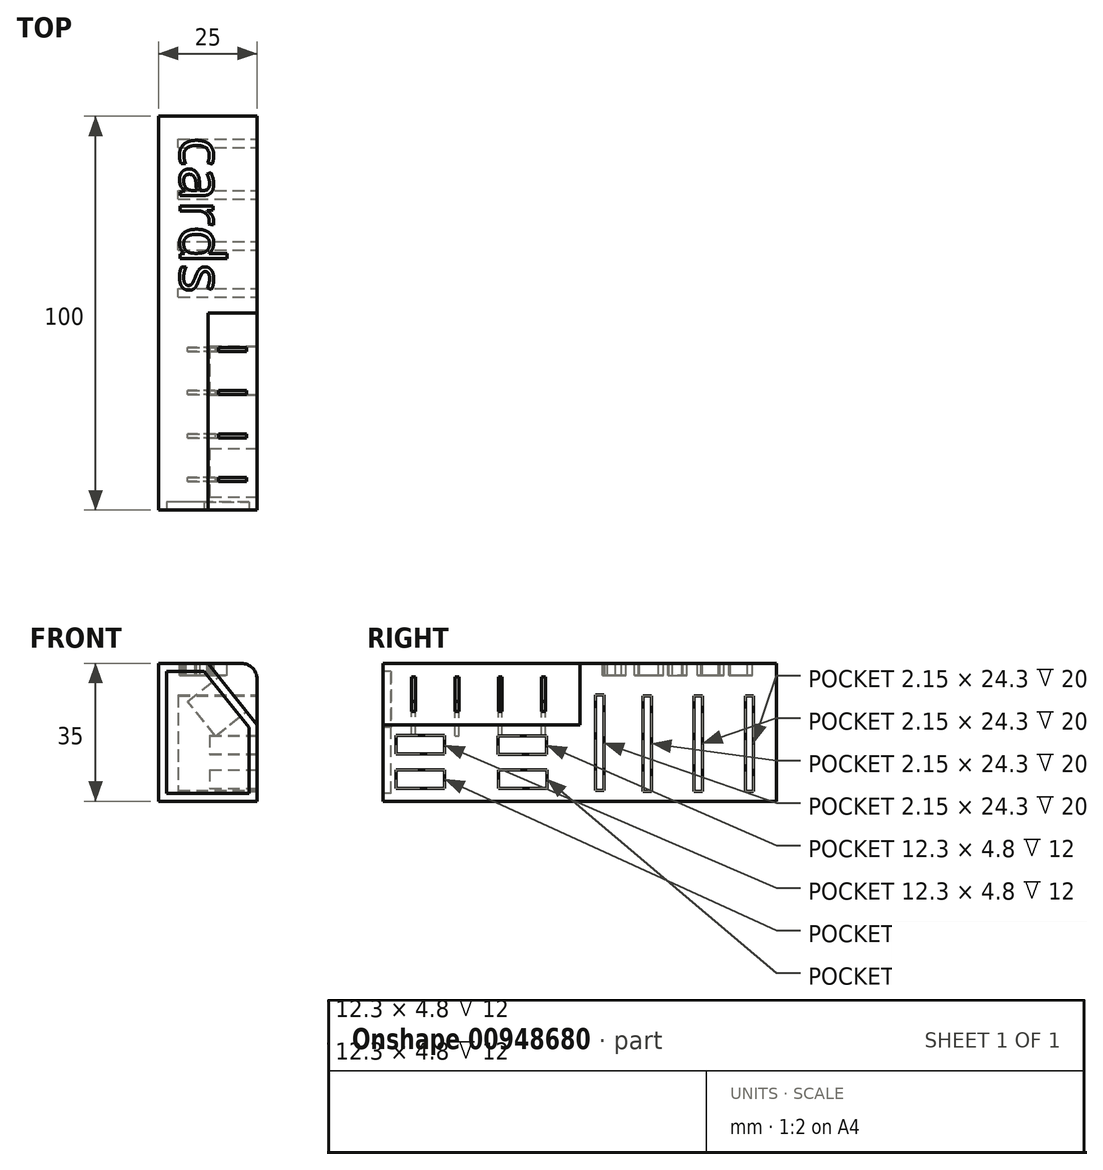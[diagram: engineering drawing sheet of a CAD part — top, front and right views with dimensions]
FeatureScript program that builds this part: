
annotation { "Feature Type Name" : "Feature", "Feature Type Description" : "" }
export const myFeature = defineFeature(function(context is Context, id is Id, definition is map)
    precondition{}
    {
        {
            var Q0;
            Q0=qCreatedBy(makeId("Top.planeOp"),FACE);
            var sketch = newSketch(context, id + "F0", { "sketchPlane" : qUnion([Q0])});
            skLineSegment(sketch, "E0.bottom", {"start": v(12.5, 50) * mm, "end": v(-12.5, 50) * mm});
            skLineSegment(sketch, "E0.top", {"start": v(12.5, -50) * mm, "end": v(-12.5, -50) * mm});
            skLineSegment(sketch, "E0.left", {"start": v(12.5, 50) * mm, "end": v(12.5, -50) * mm});
            skLineSegment(sketch, "E0.right", {"start": v(-12.5, 50) * mm, "end": v(-12.5, -50) * mm});
            skPoint(sketch, "E0.middle", {"position": v(0, 0) * mm});
            skSolve(sketch);
        }
        {
            var Q0;
            Q0=makeQuery(id+"F0.imprint","IMPRINT",FACE,{"disambiguationData":[TD([[makeQuery(id+"F0.imprint","IMPRINT",EDGE,{"derivedFrom":sQuery(id+"F0.wireOp",EDGE,"E0.bottom")}),1.0]])]});
            extrude(context, id + "F1", {"entities" : qUnion([Q0]), "oppositeDirection" : true, "depth" : 35 * mm, "offsetDistance" : 25 * mm});
        }
        {
            var Q0;
            Q0=makeQuery(id+"F1.opExtrude","SWEPT_FACE",FACE,{"disambiguationData":[OSD([sQuery(id+"F0.wireOp",EDGE,"E0.top")])]});
            var sketch = newSketch(context, id + "F2", { "sketchPlane" : qUnion([Q0])});
            skLineSegment(sketch, "E1", {"start": v(0, 0) * mm, "end": v(12.5, -15.61) * mm});
            skSolve(sketch);
        }
        {
            var Q0;
            {var subQ0=sQuery(id+"F2.wireOp",EDGE,"E1");Q0=makeQuery(id+"F2.imprint","IMPRINT",FACE,{"disambiguationData":[TD([[makeQuery(id+"F2.imprint","IMPRINT",EDGE,{"derivedFrom":subQ0}),1.0]])]});}
            extrude(context, id + "F3", {"entities" : qUnion([Q0]), "operationType" : NewBodyOperationType.REMOVE, "oppositeDirection" : true, "depth" : 50 * mm, "offsetDistance" : 25 * mm});
        }
        {
            var Q0;
            Q0=makeQuery(id+"F3.boolean.opBoolean","COPY",FACE,{"derivedFrom":makeQuery(id+"F3.opExtrude","SWEPT_FACE",FACE,{"disambiguationData":[OSD([sQuery(id+"F2.wireOp",EDGE,"E1")])]})});
            var sketch = newSketch(context, id + "F4", { "sketchPlane" : qUnion([Q0])});
            skLineSegment(sketch, "E2", {"start": v(-50, -10) * mm, "end": v(0, -10) * mm, "construction": true});
            skLineSegment(sketch, "E3.bottom", {"start": v(-9.72, -15.65) * mm, "end": v(-8.72, -15.65) * mm});
            skLineSegment(sketch, "E3.top", {"start": v(-9.72, -4.35) * mm, "end": v(-8.72, -4.35) * mm});
            skLineSegment(sketch, "E3.left", {"start": v(-9.72, -15.65) * mm, "end": v(-9.72, -4.35) * mm});
            skLineSegment(sketch, "E3.right", {"start": v(-8.72, -15.65) * mm, "end": v(-8.72, -4.35) * mm});
            skPoint(sketch, "E3.middle", {"position": v(-9.22, -10) * mm});
            skLineSegment(sketch, "E4.1.0.0", {"start": v(-20.72, -4.35) * mm, "end": v(-19.72, -4.35) * mm});
            skLineSegment(sketch, "E4.1.0.1", {"start": v(-19.72, -15.65) * mm, "end": v(-19.72, -4.35) * mm});
            skLineSegment(sketch, "E4.1.0.2", {"start": v(-20.72, -15.65) * mm, "end": v(-20.72, -4.35) * mm});
            skLineSegment(sketch, "E4.1.0.3", {"start": v(-20.72, -15.65) * mm, "end": v(-19.72, -15.65) * mm});
            skLineSegment(sketch, "E4.2.0.0", {"start": v(-31.72, -4.35) * mm, "end": v(-30.72, -4.35) * mm});
            skLineSegment(sketch, "E4.2.0.1", {"start": v(-30.72, -15.65) * mm, "end": v(-30.72, -4.35) * mm});
            skLineSegment(sketch, "E4.2.0.2", {"start": v(-31.72, -15.65) * mm, "end": v(-31.72, -4.35) * mm});
            skLineSegment(sketch, "E4.2.0.3", {"start": v(-31.72, -15.65) * mm, "end": v(-30.72, -15.65) * mm});
            skLineSegment(sketch, "E4.3.0.0", {"start": v(-42.72, -4.35) * mm, "end": v(-41.72, -4.35) * mm});
            skLineSegment(sketch, "E4.3.0.1", {"start": v(-41.72, -15.65) * mm, "end": v(-41.72, -4.35) * mm});
            skLineSegment(sketch, "E4.3.0.2", {"start": v(-42.72, -15.65) * mm, "end": v(-42.72, -4.35) * mm});
            skLineSegment(sketch, "E4.3.0.3", {"start": v(-42.72, -15.65) * mm, "end": v(-41.72, -15.65) * mm});
            skLineSegment(sketch, "E4.direction1", {"start": v(-9.72, -4.35) * mm, "end": v(-20.72, -4.35) * mm, "construction": true});
            skSolve(sketch);
        }
        {
            var Q0;
            Q0=makeQuery(id+"F4.imprint","IMPRINT",FACE,{"disambiguationData":[TD([[makeQuery(id+"F4.imprint","IMPRINT",EDGE,{"derivedFrom":sQuery(id+"F4.wireOp",EDGE,"E3.bottom")}),1.0]])]});
            var Q1;
            Q1=makeQuery(id+"F4.imprint","IMPRINT",FACE,{"disambiguationData":[TD([[makeQuery(id+"F4.imprint","IMPRINT",EDGE,{"derivedFrom":sQuery(id+"F4.wireOp",EDGE,"E4.1.0.0")}),-1.0]])]});
            var Q2;
            Q2=makeQuery(id+"F4.imprint","IMPRINT",FACE,{"disambiguationData":[TD([[makeQuery(id+"F4.imprint","IMPRINT",EDGE,{"derivedFrom":sQuery(id+"F4.wireOp",EDGE,"E4.2.0.0")}),-1.0]])]});
            var Q3;
            Q3=makeQuery(id+"F4.imprint","IMPRINT",FACE,{"disambiguationData":[TD([[makeQuery(id+"F4.imprint","IMPRINT",EDGE,{"derivedFrom":sQuery(id+"F4.wireOp",EDGE,"E4.3.0.0")}),-1.0]])]});
            extrude(context, id + "F5", {"entities" : qUnion([Q0, Q1, Q2, Q3]), "operationType" : NewBodyOperationType.REMOVE, "oppositeDirection" : true, "depth" : 10 * mm, "offsetDistance" : 25 * mm});
        }
        {
            var Q0;
            Q0=makeQuery(id+"F1.opExtrude","CAP_EDGE",EDGE,{"disambiguationData":[OSD([sQuery(id+"F0.wireOp",EDGE,"E0.left")])],"isStart":true});
            fillet(context, id + "F6", {"entities" : qUnion([Q0]), "radius" : 4 * mm, "tangentPropagation" : true, "allowEdgeOverflow" : false});
        }
        {
            var Q0;
            Q0=makeQuery(id+"F1.opExtrude","SWEPT_FACE",FACE,{"disambiguationData":[OSD([sQuery(id+"F0.wireOp",EDGE,"E0.left")])]});
            var sketch = newSketch(context, id + "F7", { "sketchPlane" : qUnion([Q0])});
            skLineSegment(sketch, "E5.bottom", {"start": v(42.02, -8.21) * mm, "end": v(44.17, -8.21) * mm});
            skLineSegment(sketch, "E5.top", {"start": v(42.02, -32.51) * mm, "end": v(44.17, -32.51) * mm});
            skLineSegment(sketch, "E5.left", {"start": v(42.02, -8.21) * mm, "end": v(42.02, -32.51) * mm});
            skLineSegment(sketch, "E5.right", {"start": v(44.17, -8.21) * mm, "end": v(44.17, -32.51) * mm});
            skPoint(sketch, "E5.middle", {"position": v(43.1, -20.36) * mm});
            skLineSegment(sketch, "E6.bottom", {"start": v(-34.37, -27) * mm, "end": v(-46.67, -27) * mm});
            skLineSegment(sketch, "E6.top", {"start": v(-34.37, -31.8) * mm, "end": v(-46.67, -31.8) * mm});
            skLineSegment(sketch, "E6.left", {"start": v(-34.37, -27) * mm, "end": v(-34.37, -31.8) * mm});
            skLineSegment(sketch, "E6.right", {"start": v(-46.67, -27) * mm, "end": v(-46.67, -31.8) * mm});
            skPoint(sketch, "E6.middle", {"position": v(-40.52, -29.4) * mm});
            skLineSegment(sketch, "E7.1.0.0", {"start": v(29.02, -8.21) * mm, "end": v(31.17, -8.21) * mm});
            skLineSegment(sketch, "E7.1.0.1", {"start": v(31.17, -8.21) * mm, "end": v(31.17, -32.51) * mm});
            skLineSegment(sketch, "E7.1.0.2", {"start": v(29.02, -8.21) * mm, "end": v(29.02, -32.51) * mm});
            skLineSegment(sketch, "E7.1.0.3", {"start": v(29.02, -32.51) * mm, "end": v(31.17, -32.51) * mm});
            skLineSegment(sketch, "E7.2.0.0", {"start": v(16.02, -8.21) * mm, "end": v(18.17, -8.21) * mm});
            skLineSegment(sketch, "E7.2.0.1", {"start": v(18.17, -8.21) * mm, "end": v(18.17, -32.51) * mm});
            skLineSegment(sketch, "E7.2.0.2", {"start": v(16.02, -8.21) * mm, "end": v(16.02, -32.51) * mm});
            skLineSegment(sketch, "E7.2.0.3", {"start": v(16.02, -32.51) * mm, "end": v(18.17, -32.51) * mm});
            skLineSegment(sketch, "E7.3.0.0", {"start": v(4.04, -8.01) * mm, "end": v(6.2, -8.01) * mm});
            skLineSegment(sketch, "E7.3.0.1", {"start": v(6.2, -8.01) * mm, "end": v(6.2, -32.31) * mm});
            skLineSegment(sketch, "E7.3.0.2", {"start": v(4.04, -8.01) * mm, "end": v(4.04, -32.31) * mm});
            skLineSegment(sketch, "E7.3.0.3", {"start": v(4.04, -32.31) * mm, "end": v(6.2, -32.31) * mm});
            skLineSegment(sketch, "E8.1.0.0", {"start": v(-8.37, -31.8) * mm, "end": v(-20.67, -31.8) * mm});
            skLineSegment(sketch, "E8.1.0.1", {"start": v(-20.67, -27) * mm, "end": v(-20.67, -31.8) * mm});
            skLineSegment(sketch, "E8.1.0.2", {"start": v(-8.37, -27) * mm, "end": v(-20.67, -27) * mm});
            skLineSegment(sketch, "E8.1.0.3", {"start": v(-8.37, -27) * mm, "end": v(-8.37, -31.8) * mm});
            skLineSegment(sketch, "E8.direction1", {"start": v(-46.67, -31.8) * mm, "end": v(-20.67, -31.8) * mm, "construction": true});
            skLineSegment(sketch, "E9.bottom", {"start": v(-34.37, -18.25) * mm, "end": v(-46.67, -18.25) * mm});
            skLineSegment(sketch, "E9.top", {"start": v(-34.37, -23.05) * mm, "end": v(-46.67, -23.05) * mm});
            skLineSegment(sketch, "E9.left", {"start": v(-34.37, -18.25) * mm, "end": v(-34.37, -23.05) * mm});
            skLineSegment(sketch, "E9.right", {"start": v(-46.67, -18.25) * mm, "end": v(-46.67, -23.05) * mm});
            skPoint(sketch, "E9.middle", {"position": v(-40.52, -20.65) * mm});
            skLineSegment(sketch, "E10.1.0.0", {"start": v(-8.47, -23.17) * mm, "end": v(-20.77, -23.17) * mm});
            skLineSegment(sketch, "E10.1.0.1", {"start": v(-20.77, -18.37) * mm, "end": v(-20.77, -23.17) * mm});
            skLineSegment(sketch, "E10.1.0.2", {"start": v(-8.47, -18.37) * mm, "end": v(-20.77, -18.37) * mm});
            skLineSegment(sketch, "E10.1.0.3", {"start": v(-8.47, -18.37) * mm, "end": v(-8.47, -23.17) * mm});
            skSolve(sketch);
        }
        {
            var Q0;
            Q0=makeQuery(id+"F7.imprint","IMPRINT",FACE,{"disambiguationData":[TD([[makeQuery(id+"F7.imprint","IMPRINT",EDGE,{"derivedFrom":sQuery(id+"F7.wireOp",EDGE,"E7.3.0.0")}),-1.0]])]});
            var Q1;
            Q1=makeQuery(id+"F7.imprint","IMPRINT",FACE,{"disambiguationData":[TD([[makeQuery(id+"F7.imprint","IMPRINT",EDGE,{"derivedFrom":sQuery(id+"F7.wireOp",EDGE,"E7.2.0.0")}),-1.0]])]});
            var Q2;
            Q2=makeQuery(id+"F7.imprint","IMPRINT",FACE,{"disambiguationData":[TD([[makeQuery(id+"F7.imprint","IMPRINT",EDGE,{"derivedFrom":sQuery(id+"F7.wireOp",EDGE,"E7.1.0.0")}),-1.0]])]});
            var Q3;
            Q3=makeQuery(id+"F7.imprint","IMPRINT",FACE,{"disambiguationData":[TD([[makeQuery(id+"F7.imprint","IMPRINT",EDGE,{"derivedFrom":sQuery(id+"F7.wireOp",EDGE,"E5.bottom")}),-1.0]])]});
            extrude(context, id + "F8", {"entities" : qUnion([Q0, Q1, Q2, Q3]), "operationType" : NewBodyOperationType.REMOVE, "oppositeDirection" : true, "depth" : 20 * mm, "offsetDistance" : 25 * mm});
        }
        {
            var Q0;
            Q0=makeQuery(id+"F7.imprint","IMPRINT",FACE,{"disambiguationData":[TD([[makeQuery(id+"F7.imprint","IMPRINT",EDGE,{"derivedFrom":sQuery(id+"F7.wireOp",EDGE,"E6.bottom")}),1.0]])]});
            var Q1;
            Q1=makeQuery(id+"F7.imprint","IMPRINT",FACE,{"disambiguationData":[TD([[makeQuery(id+"F7.imprint","IMPRINT",EDGE,{"derivedFrom":sQuery(id+"F7.wireOp",EDGE,"E8.1.0.0")}),-1.0]])]});
            var Q2;
            Q2=makeQuery(id+"F7.imprint","IMPRINT",FACE,{"disambiguationData":[TD([[makeQuery(id+"F7.imprint","IMPRINT",EDGE,{"derivedFrom":sQuery(id+"F7.wireOp",EDGE,"E9.bottom")}),1.0]])]});
            var Q3;
            Q3=makeQuery(id+"F7.imprint","IMPRINT",FACE,{"disambiguationData":[TD([[makeQuery(id+"F7.imprint","IMPRINT",EDGE,{"derivedFrom":sQuery(id+"F7.wireOp",EDGE,"E10.1.0.0")}),-1.0]])]});
            extrude(context, id + "F9", {"entities" : qUnion([Q0, Q1, Q2, Q3]), "operationType" : NewBodyOperationType.REMOVE, "oppositeDirection" : true, "depth" : 12 * mm, "offsetDistance" : 25 * mm});
        }
        {
            var Q0;
            Q0=makeQuery(id+"F1.opExtrude","CAP_FACE",FACE,{"disambiguationData":[OSD([sQuery(id+"F0.wireOp",EDGE,"E0.bottom"),sQuery(id+"F0.wireOp",EDGE,"E0.top"),sQuery(id+"F0.wireOp",EDGE,"E0.left"),sQuery(id+"F0.wireOp",EDGE,"E0.right")])],"isStart":true});
            var sketch = newSketch(context, id + "F10", { "sketchPlane" : qUnion([Q0])});
            skText(sketch, "E11", { "text": "cards", "fontName": "OpenSans-Regular.ttf"});
            skPoint(sketch, "E12", {"position": v(4.25, 0) * mm});
            const initialGuessF10  = {"E11": [-0.00705, 0.0448, 0, -1, 0.0113]};
            skSetInitialGuess(sketch, initialGuessF10);
            skSolve(sketch);
        }
        {
            var Q0;
            Q0 = qSketchRegion(id + "F10", true);
            extrude(context, id + "F11", {"entities" : qUnion([Q0]), "operationType" : NewBodyOperationType.REMOVE, "oppositeDirection" : true, "depth" : 3 * mm, "offsetDistance" : 25 * mm});
        }
        {
            var Q0;
            Q0=makeQuery(id+"F1.opExtrude","SWEPT_FACE",FACE,{"disambiguationData":[OSD([sQuery(id+"F0.wireOp",EDGE,"E0.top")])]});
            var sketch = newSketch(context, id + "F12", { "sketchPlane" : qUnion([Q0])});
            skLineSegment(sketch, "E13.0", {"start": v(-0.96, -2) * mm, "end": v(10.5, -16.31) * mm});
            skLineSegment(sketch, "E13.1", {"start": v(10.5, -33) * mm, "end": v(10.5, -16.31) * mm});
            skLineSegment(sketch, "E13.2", {"start": v(-0.96, -2) * mm, "end": v(-10.5, -2) * mm});
            skLineSegment(sketch, "E13.3", {"start": v(-10.5, -33) * mm, "end": v(-10.5, -2) * mm});
            skLineSegment(sketch, "E13.4", {"start": v(10.5, -33) * mm, "end": v(-10.5, -33) * mm});
            skSolve(sketch);
        }
        {
            var Q0;
            Q0=makeQuery(id+"F12.imprint","IMPRINT",FACE,{"disambiguationData":[TD([[makeQuery(id+"F12.imprint","IMPRINT",EDGE,{"derivedFrom":sQuery(id+"F12.wireOp",EDGE,"E13.0")}),-1.0]])]});
            extrude(context, id + "F13", {"entities" : qUnion([Q0]), "operationType" : NewBodyOperationType.REMOVE, "oppositeDirection" : true, "depth" : 2 * mm, "offsetDistance" : 25 * mm});
        }
    });
